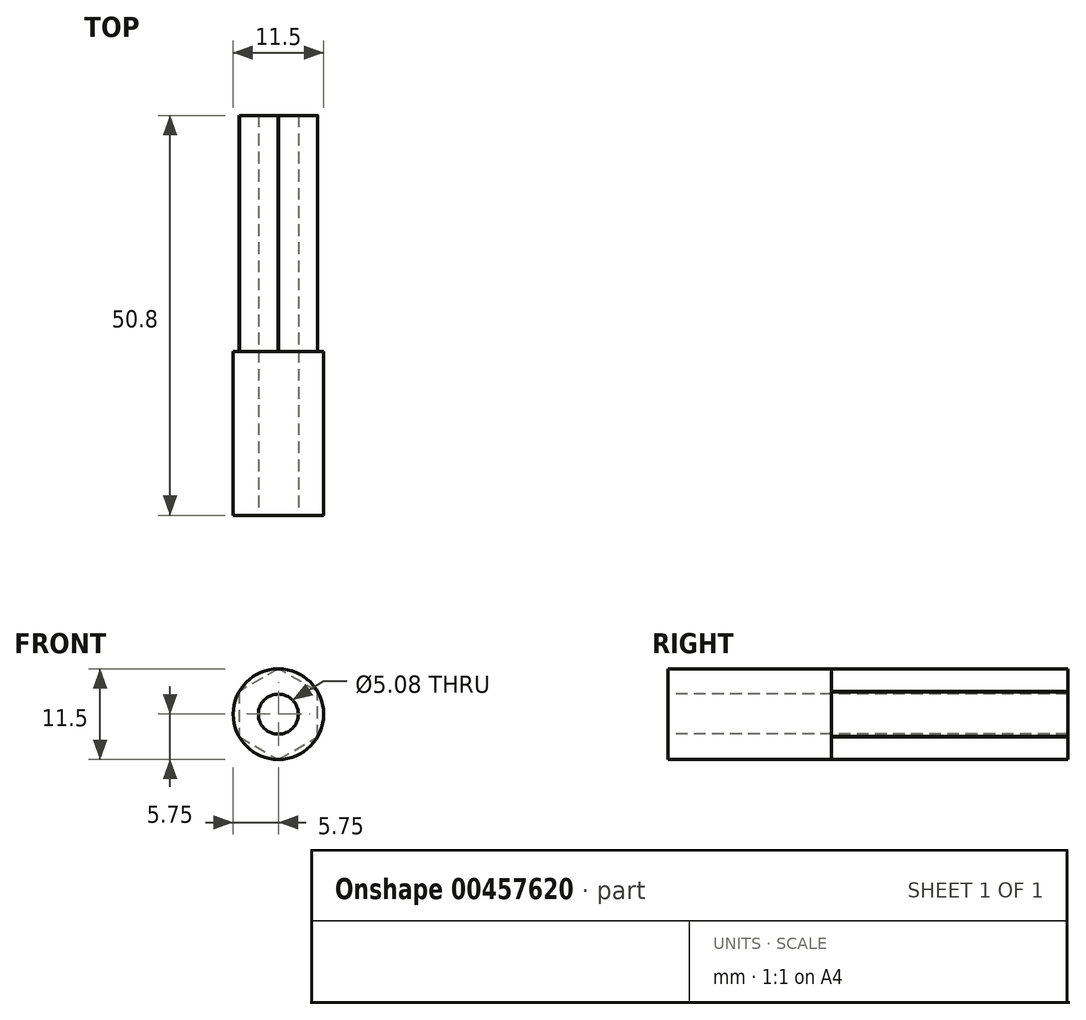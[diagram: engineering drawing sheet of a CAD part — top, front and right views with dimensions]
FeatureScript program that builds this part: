
annotation { "Feature Type Name" : "Feature", "Feature Type Description" : "" }
export const myFeature = defineFeature(function(context is Context, id is Id, definition is map)
    precondition{}
    {
        {
            var Q0;
            Q0=qCreatedBy(makeId("Front.planeOp"),FACE);
            var sketch = newSketch(context, id + "F0", { "sketchPlane" : qUnion([Q0])});
            skCircle(sketch, "E0", {"center": v(0, 0) * mm, "radius": 2.54 * mm});
            skCircle(sketch, "E1", {"center": v(0, 0) * mm, "radius": 5.75 * mm});
            skLineSegment(sketch, "E2", {"start": v(0, 0) * mm, "end": v(0, 5.75) * mm});
            skLineSegment(sketch, "E3", {"start": v(0, 5.75) * mm, "end": v(0, 0) * mm});
            skLineSegment(sketch, "E4", {"start": v(1.1, 5.64) * mm, "end": v(1.1, 8.18) * mm});
            skLineSegment(sketch, "E5", {"start": v(-1.1, 5.64) * mm, "end": v(-1.1, 8.18) * mm});
            skLineSegment(sketch, "E6", {"start": v(-1.1, 5.64) * mm, "end": v(0, 5.64) * mm});
            skLineSegment(sketch, "E7", {"start": v(0, 5.64) * mm, "end": v(1.1, 5.64) * mm});
            skLineSegment(sketch, "E8.1.0", {"start": v(-3.73, 5.53) * mm, "end": v(-5.53, 7.32) * mm});
            skLineSegment(sketch, "E8.1.2", {"start": v(-5.53, 3.73) * mm, "end": v(-7.32, 5.53) * mm});
            skLineSegment(sketch, "E8.1.3", {"start": v(-5.53, 3.73) * mm, "end": v(-4.63, 4.63) * mm});
            skLineSegment(sketch, "E8.1.4", {"start": v(-4.63, 4.63) * mm, "end": v(-3.73, 5.53) * mm});
            skLineSegment(sketch, "E8.2.0", {"start": v(-6.55, 1.27) * mm, "end": v(-9.09, 1.27) * mm});
            skLineSegment(sketch, "E8.2.2", {"start": v(-6.55, -1.27) * mm, "end": v(-9.09, -1.27) * mm});
            skLineSegment(sketch, "E8.2.3", {"start": v(-6.55, -1.27) * mm, "end": v(-6.55, 0) * mm});
            skLineSegment(sketch, "E8.2.4", {"start": v(-6.55, 0) * mm, "end": v(-6.55, 1.27) * mm});
            skLineSegment(sketch, "E8.3.0", {"start": v(-5.53, -3.73) * mm, "end": v(-7.32, -5.53) * mm});
            skLineSegment(sketch, "E8.3.2", {"start": v(-3.73, -5.53) * mm, "end": v(-5.53, -7.32) * mm});
            skLineSegment(sketch, "E8.3.3", {"start": v(-3.73, -5.53) * mm, "end": v(-4.63, -4.63) * mm});
            skLineSegment(sketch, "E8.3.4", {"start": v(-4.63, -4.63) * mm, "end": v(-5.53, -3.73) * mm});
            skLineSegment(sketch, "E8.4.0", {"start": v(-1.27, -6.55) * mm, "end": v(-1.27, -9.09) * mm});
            skLineSegment(sketch, "E8.4.2", {"start": v(1.27, -6.55) * mm, "end": v(1.27, -9.09) * mm});
            skLineSegment(sketch, "E8.4.3", {"start": v(1.27, -6.55) * mm, "end": v(0, -6.55) * mm});
            skLineSegment(sketch, "E8.4.4", {"start": v(0, -6.55) * mm, "end": v(-1.27, -6.55) * mm});
            skLineSegment(sketch, "E8.5.0", {"start": v(3.73, -5.53) * mm, "end": v(5.53, -7.32) * mm});
            skLineSegment(sketch, "E8.5.2", {"start": v(5.53, -3.73) * mm, "end": v(7.32, -5.53) * mm});
            skLineSegment(sketch, "E8.5.3", {"start": v(5.53, -3.73) * mm, "end": v(4.63, -4.63) * mm});
            skLineSegment(sketch, "E8.5.4", {"start": v(4.63, -4.63) * mm, "end": v(3.73, -5.53) * mm});
            skLineSegment(sketch, "E8.6.0", {"start": v(6.55, -1.27) * mm, "end": v(9.09, -1.27) * mm});
            skLineSegment(sketch, "E8.6.2", {"start": v(6.55, 1.27) * mm, "end": v(9.09, 1.27) * mm});
            skLineSegment(sketch, "E8.6.3", {"start": v(6.55, 1.27) * mm, "end": v(6.55, 0) * mm});
            skLineSegment(sketch, "E8.6.4", {"start": v(6.55, 0) * mm, "end": v(6.55, -1.27) * mm});
            skLineSegment(sketch, "E8.7.0", {"start": v(5.53, 3.73) * mm, "end": v(7.32, 5.53) * mm});
            skLineSegment(sketch, "E8.7.2", {"start": v(3.73, 5.53) * mm, "end": v(5.53, 7.32) * mm});
            skLineSegment(sketch, "E8.7.3", {"start": v(3.73, 5.53) * mm, "end": v(4.63, 4.63) * mm});
            skLineSegment(sketch, "E8.7.4", {"start": v(4.63, 4.63) * mm, "end": v(5.53, 3.73) * mm});
            skLineSegment(sketch, "E9", {"start": v(-1.1, 8.18) * mm, "end": v(1.1, 8.18) * mm});
            skLineSegment(sketch, "E10", {"start": v(5.53, 7.32) * mm, "end": v(7.32, 5.53) * mm});
            skLineSegment(sketch, "E11", {"start": v(9.09, 1.27) * mm, "end": v(9.09, -1.27) * mm});
            skLineSegment(sketch, "E12", {"start": v(7.32, -5.53) * mm, "end": v(5.53, -7.32) * mm});
            skLineSegment(sketch, "E13", {"start": v(-5.53, 7.32) * mm, "end": v(-7.32, 5.53) * mm});
            skLineSegment(sketch, "E14", {"start": v(-9.09, 1.27) * mm, "end": v(-9.09, -1.27) * mm});
            skLineSegment(sketch, "E15", {"start": v(-7.32, -5.53) * mm, "end": v(-5.53, -7.32) * mm});
            skLineSegment(sketch, "E16", {"start": v(-1.27, -9.09) * mm, "end": v(1.27, -9.09) * mm});
            skSolve(sketch);
        }
        {
            var Q0;
            {var subQ3=sQuery(id+"F0.wireOp",EDGE,"E7");Q0=makeQuery(id+"F0.imprint","IMPRINT",FACE,{"disambiguationData":[TD([[makeQuery(id+"F0.imprint","IMPRINT",EDGE,{"derivedFrom":subQ3}),1.0]])]});}
            var Q1;
            {var subQ3=sQuery(id+"F0.wireOp",EDGE,"E6");Q1=makeQuery(id+"F0.imprint","IMPRINT",FACE,{"disambiguationData":[TD([[makeQuery(id+"F0.imprint","IMPRINT",EDGE,{"derivedFrom":subQ3}),1.0]])]});}
            var Q2;
            Q2=makeQuery(id+"F0.imprint","IMPRINT",FACE,{"disambiguationData":[TD([[makeQuery(id+"F0.imprint","IMPRINT",EDGE,{"derivedFrom":sQuery(id+"F0.wireOp",EDGE,"E0")}),-1.0]])]});
            extrude(context, id + "F1", {"entities" : qUnion([Q0, Q1, Q2]), "oppositeDirection" : true, "depth" : 50.8 * mm});
        }
        {
            var Q0;
            Q0=makeQuery(id+"F1.opExtrude","CAP_FACE",FACE,{"disambiguationData":[OSD([sQuery(id+"F0.wireOp",EDGE,"E0"),sQuery(id+"F0.wireOp",EDGE,"E1")])],"isStart":false});
            var sketch = newSketch(context, id + "F2", { "sketchPlane" : qUnion([Q0])});
            skCircle(sketch, "E17.cCircle", {"center": v(0, 0) * mm, "radius": 5 * mm, "construction": true});
            skLineSegment(sketch, "E17.0", {"start": v(5, 2.89) * mm, "end": v(5, -2.89) * mm});
            skLineSegment(sketch, "E17.1", {"start": v(5, -2.89) * mm, "end": v(0, -5.77) * mm});
            skLineSegment(sketch, "E17.2", {"start": v(0, -5.77) * mm, "end": v(-5, -2.89) * mm});
            skLineSegment(sketch, "E17.3", {"start": v(-5, -2.89) * mm, "end": v(-5, 2.89) * mm});
            skLineSegment(sketch, "E17.4", {"start": v(-5, 2.89) * mm, "end": v(0, 5.77) * mm});
            skLineSegment(sketch, "E17.5", {"start": v(0, 5.77) * mm, "end": v(5, 2.89) * mm});
            skPoint(sketch, "E17.0.midPoint", {"position": v(5, 0) * mm});
            skLineSegment(sketch, "E18.bottom", {"start": v(10.15, -10.28) * mm, "end": v(-10.15, -10.28) * mm});
            skLineSegment(sketch, "E18.top", {"start": v(10.15, 10.28) * mm, "end": v(-10.15, 10.28) * mm});
            skLineSegment(sketch, "E18.left", {"start": v(10.15, -10.28) * mm, "end": v(10.15, 10.28) * mm});
            skLineSegment(sketch, "E18.right", {"start": v(-10.15, -10.28) * mm, "end": v(-10.15, 10.28) * mm});
            skSolve(sketch);
        }
        {
            var Q0;
            Q0 = qSketchRegion(id + "F2", true);
            extrude(context, id + "F3", {"entities" : qUnion([Q0]), "operationType" : NewBodyOperationType.REMOVE, "oppositeDirection" : true, "depth" : 30 * mm});
        }
    });
